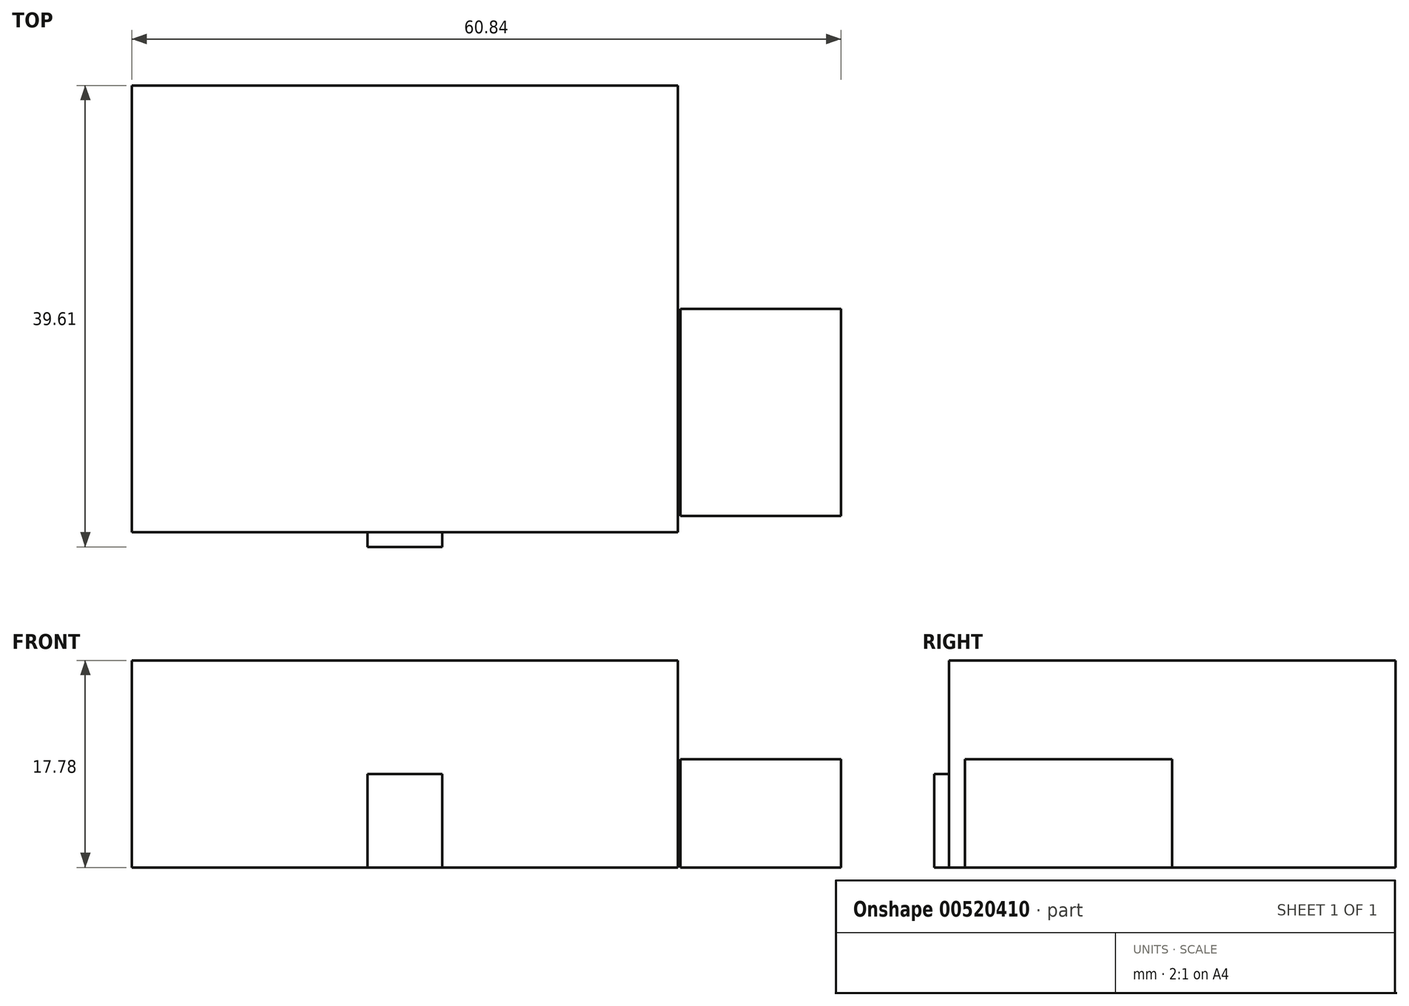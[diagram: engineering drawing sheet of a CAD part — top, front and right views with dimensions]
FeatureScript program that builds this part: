
annotation { "Feature Type Name" : "Feature", "Feature Type Description" : "" }
export const myFeature = defineFeature(function(context is Context, id is Id, definition is map)
    precondition{}
    {
        {
            var Q0;
            Q0=qCreatedBy(makeId("Top.planeOp"),FACE);
            var sketch = newSketch(context, id + "F0", { "sketchPlane" : qUnion([Q0])});
            skLineSegment(sketch, "E0.bottom", {"start": v(-23.42, 19.17) * mm, "end": v(23.42, 19.17) * mm});
            skLineSegment(sketch, "E0.top", {"start": v(-23.42, -19.17) * mm, "end": v(23.42, -19.17) * mm});
            skLineSegment(sketch, "E0.left", {"start": v(-23.42, 19.17) * mm, "end": v(-23.42, -19.17) * mm});
            skLineSegment(sketch, "E0.right", {"start": v(23.42, 19.17) * mm, "end": v(23.42, -19.17) * mm});
            skPoint(sketch, "E0.middle", {"position": v(0, 0) * mm});
            skSolve(sketch);
        }
        {
            var Q0;
            Q0=makeQuery(id+"F0.imprint","IMPRINT",FACE,{"disambiguationData":[TD([[makeQuery(id+"F0.imprint","IMPRINT",EDGE,{"derivedFrom":sQuery(id+"F0.wireOp",EDGE,"E0.bottom")}),-1.0]])]});
            extrude(context, id + "F1", {"entities" : qUnion([Q0]), "depth" : 17.78 * mm, "offsetDistance" : 25.4 * mm});
        }
        {
            var Q0;
            Q0=makeQuery(id+"F1.opExtrude","SWEPT_FACE",FACE,{"disambiguationData":[OSD([sQuery(id+"F0.wireOp",EDGE,"E0.top")])]});
            var sketch = newSketch(context, id + "F2", { "sketchPlane" : qUnion([Q0])});
            skLineSegment(sketch, "E1.bottom", {"start": v(3.21, 0) * mm, "end": v(-3.21, 0) * mm});
            skLineSegment(sketch, "E1.top", {"start": v(3.21, 8.04) * mm, "end": v(-3.21, 8.04) * mm});
            skLineSegment(sketch, "E1.left", {"start": v(3.21, 0) * mm, "end": v(3.21, 8.04) * mm});
            skLineSegment(sketch, "E1.right", {"start": v(-3.21, 0) * mm, "end": v(-3.21, 8.04) * mm});
            skPoint(sketch, "E1.middle", {"position": v(0, 4.02) * mm});
            skSolve(sketch);
        }
        {
            var Q0;
            Q0=makeQuery(id+"F2.imprint","IMPRINT",FACE,{"disambiguationData":[TD([[makeQuery(id+"F2.imprint","IMPRINT",EDGE,{"derivedFrom":sQuery(id+"F2.wireOp",EDGE,"E1.bottom")}),1.0]])]});
            extrude(context, id + "F3", {"entities" : qUnion([Q0]), "operationType" : NewBodyOperationType.ADD, "depth" : 1.27 * mm, "offsetDistance" : 25.4 * mm});
        }
        {
            var Q0;
            Q0=makeQuery(id+"F1.opExtrude","SWEPT_FACE",FACE,{"disambiguationData":[OSD([sQuery(id+"F0.wireOp",EDGE,"E0.left")])]});
            var sketch = newSketch(context, id + "F4", { "sketchPlane" : qUnion([Q0])});
            skLineSegment(sketch, "E2", {"start": v(-19.17, 17.78) * mm, "end": v(0, 35.24) * mm});
            skLineSegment(sketch, "E3", {"start": v(0, 35.24) * mm, "end": v(19.17, 17.78) * mm});
            skSolve(sketch);
        }
        {
            var Q0;
            Q0=qCreatedBy(makeId("Front.planeOp"),FACE);
            var sketch = newSketch(context, id + "F5", { "sketchPlane" : qUnion([Q0])});
            skLineSegment(sketch, "E4", {"start": v(23.65, 9.3) * mm, "end": v(23.65, 0) * mm});
            skLineSegment(sketch, "E5", {"start": v(23.65, 0) * mm, "end": v(37.42, 0) * mm});
            skLineSegment(sketch, "E6", {"start": v(23.65, 9.3) * mm, "end": v(37.42, 9.3) * mm});
            skLineSegment(sketch, "E7", {"start": v(37.42, 0) * mm, "end": v(37.42, 9.3) * mm});
            skSolve(sketch);
        }
        {
            var Q0;
            Q0=makeQuery(id+"F5.imprint","IMPRINT",FACE,{"disambiguationData":[TD([[makeQuery(id+"F5.imprint","IMPRINT",EDGE,{"derivedFrom":sQuery(id+"F5.wireOp",EDGE,"E4")}),1.0]])]});
            extrude(context, id + "F6", {"entities" : qUnion([Q0]), "depth" : 17.78 * mm, "offsetDistance" : 25.4 * mm});
        }
    });
